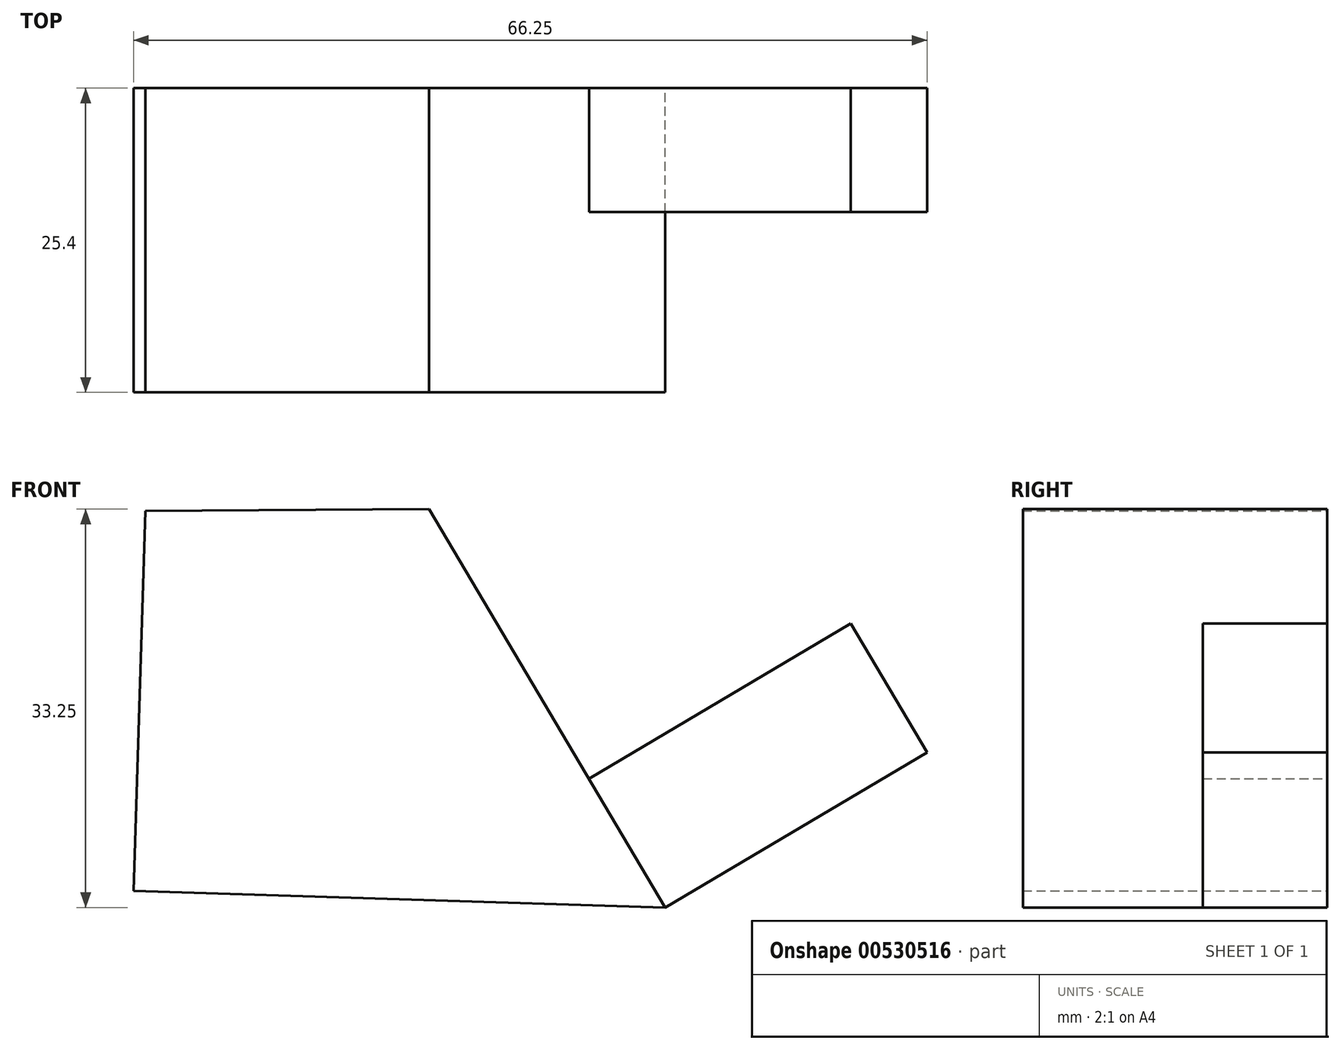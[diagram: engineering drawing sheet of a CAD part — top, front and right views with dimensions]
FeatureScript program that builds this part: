
annotation { "Feature Type Name" : "Feature", "Feature Type Description" : "" }
export const myFeature = defineFeature(function(context is Context, id is Id, definition is map)
    precondition{}
    {
        {
            var Q0;
            Q0=qCreatedBy(makeId("Front.planeOp"),FACE);
            var sketch = newSketch(context, id + "F0", { "sketchPlane" : qUnion([Q0])});
            skLineSegment(sketch, "E0", {"start": v(-25.88, 7.38) * mm, "end": v(-26.87, -24.35) * mm});
            skLineSegment(sketch, "E1", {"start": v(-26.87, -24.35) * mm, "end": v(17.53, -25.73) * mm});
            skLineSegment(sketch, "E2", {"start": v(17.53, -25.73) * mm, "end": v(18.57, 7.64) * mm});
            skLineSegment(sketch, "E3", {"start": v(18.57, 7.64) * mm, "end": v(-25.88, 7.38) * mm});
            skSolve(sketch);
        }
        {
            var Q0;
            Q0 = qSketchRegion(id + "F0", true);
            extrude(context, id + "F1", {"entities" : qUnion([Q0]), "depth" : 25.4 * mm, "offsetDistance" : 25.4 * mm});
        }
        {
            var Q0;
            Q0=makeQuery(id+"F1.opExtrude","CAP_FACE",FACE,{"disambiguationData":[OSD([sQuery(id+"F0.wireOp",EDGE,"E0"),sQuery(id+"F0.wireOp",EDGE,"E1"),sQuery(id+"F0.wireOp",EDGE,"E2"),sQuery(id+"F0.wireOp",EDGE,"E3")])],"isStart":false});
            var sketch = newSketch(context, id + "F2", { "sketchPlane" : qUnion([Q0])});
            skLineSegment(sketch, "E4", {"start": v(-2.18, 7.52) * mm, "end": v(17.53, -25.73) * mm});
            skLineSegment(sketch, "E5", {"start": v(-2.18, 7.52) * mm, "end": v(18.57, 7.64) * mm});
            skLineSegment(sketch, "E6", {"start": v(18.57, 7.64) * mm, "end": v(17.53, -25.73) * mm});
            skSolve(sketch);
        }
        {
            var Q0;
            Q0 = qSketchRegion(id + "F2", true);
            extrude(context, id + "F3", {"entities" : qUnion([Q0]), "operationType" : NewBodyOperationType.REMOVE, "oppositeDirection" : true, "depth" : 25.4 * mm, "offsetDistance" : 25.4 * mm});
        }
        {
            var Q0;
            Q0=makeQuery(id+"F3.boolean.opBoolean","COPY",FACE,{"derivedFrom":makeQuery(id+"F3.opExtrude","SWEPT_FACE",FACE,{"disambiguationData":[OSD([sQuery(id+"F2.wireOp",EDGE,"E4")])]})});
            var sketch = newSketch(context, id + "F4", { "sketchPlane" : qUnion([Q0])});
            skLineSegment(sketch, "E7", {"start": v(-10.35, -31.08) * mm, "end": v(-10.35, -18.57) * mm});
            skLineSegment(sketch, "E8", {"start": v(-10.35, -18.57) * mm, "end": v(0, -18.57) * mm});
            skLineSegment(sketch, "E9", {"start": v(0.3, -18.57) * mm, "end": v(0, -31.08) * mm});
            skLineSegment(sketch, "E10", {"start": v(0, -31.08) * mm, "end": v(-10.35, -31.08) * mm});
            skSolve(sketch);
        }
        {
            var Q0;
            Q0 = qSketchRegion(id + "F4", true);
            var Q1;
            Q1=makeQuery(id+"F4.imprint","IMPRINT",FACE,{"disambiguationData":[TD([[makeQuery(id+"F4.imprint","IMPRINT",EDGE,{"derivedFrom":sQuery(id+"F4.wireOp",EDGE,"E7")}),-1.0]])]});
            extrude(context, id + "F5", {"entities" : qUnion([Q0, Q1]), "operationType" : NewBodyOperationType.ADD, "depth" : 25.4 * mm, "offsetDistance" : 25.4 * mm});
        }
    });
